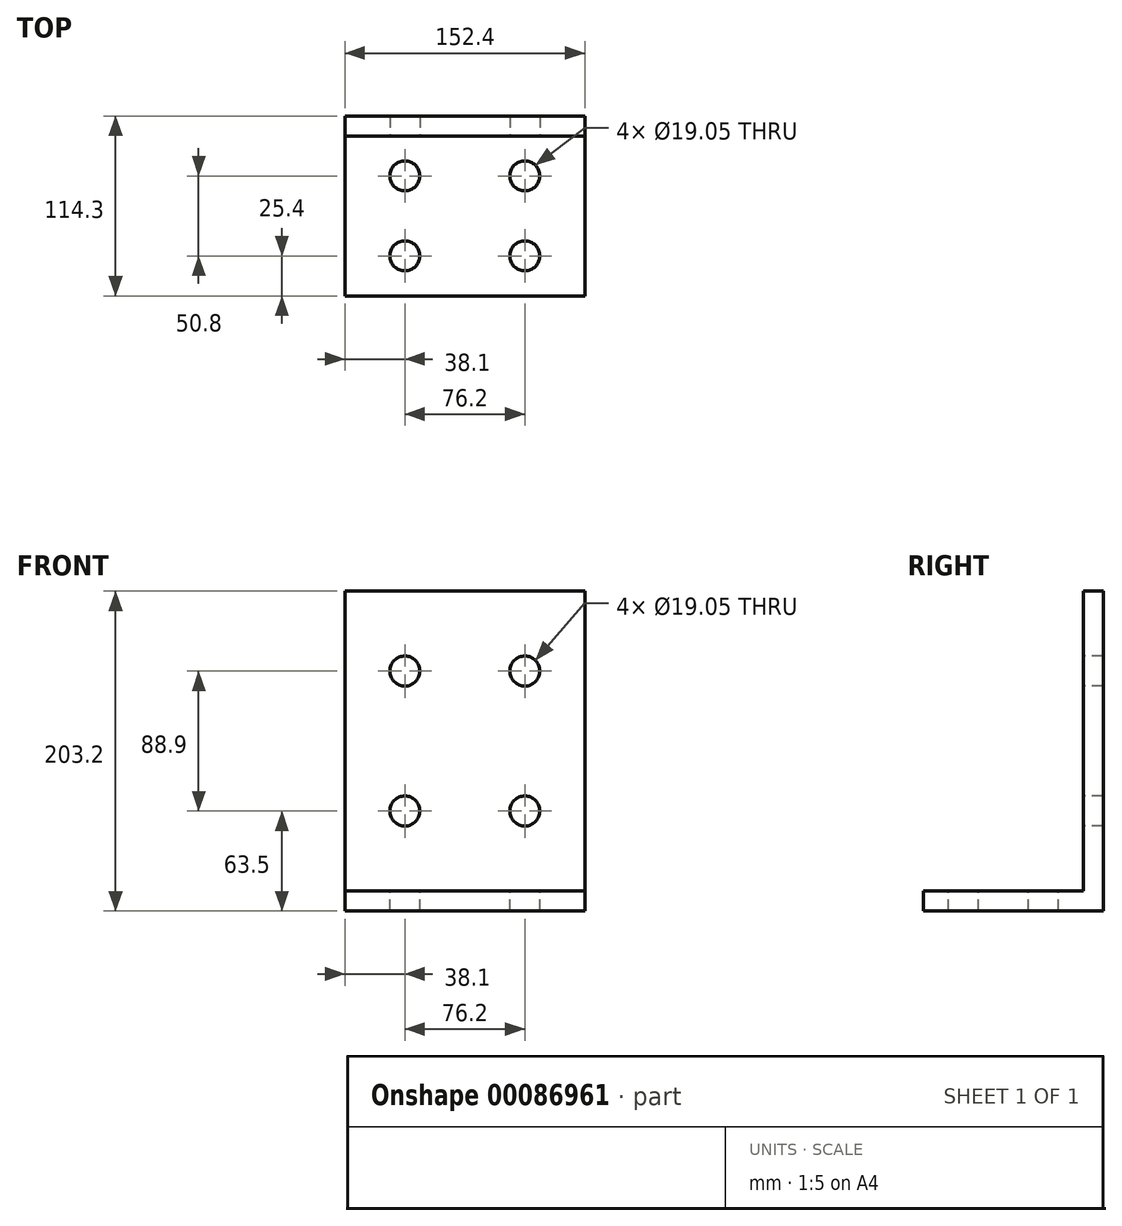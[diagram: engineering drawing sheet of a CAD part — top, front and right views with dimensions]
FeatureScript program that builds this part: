
annotation { "Feature Type Name" : "Feature", "Feature Type Description" : "" }
export const myFeature = defineFeature(function(context is Context, id is Id, definition is map)
    precondition{}
    {
        {
            var Q0;
            Q0=qCreatedBy(makeId("Front.planeOp"),FACE);
            var sketch = newSketch(context, id + "F0", { "sketchPlane" : qUnion([Q0])});
            skLineSegment(sketch, "E0.bottom", {"start": v(0, 0) * mm, "end": v(152.4, 0) * mm});
            skLineSegment(sketch, "E0.top", {"start": v(0, 203.2) * mm, "end": v(152.4, 203.2) * mm});
            skLineSegment(sketch, "E0.left", {"start": v(0, 0) * mm, "end": v(0, 203.2) * mm});
            skLineSegment(sketch, "E0.right", {"start": v(152.4, 0) * mm, "end": v(152.4, 203.2) * mm});
            skSolve(sketch);
        }
        {
            var Q0;
            Q0 = qSketchRegion(id + "F0", true);
            extrude(context, id + "F1", {"entities" : qUnion([Q0]), "depth" : 12.7 * mm});
        }
        {
            var Q0;
            Q0=makeQuery(id+"F1.opExtrude","CAP_FACE",FACE,{"disambiguationData":[OSD([sQuery(id+"F0.wireOp",EDGE,"E0.bottom"),sQuery(id+"F0.wireOp",EDGE,"E0.top"),sQuery(id+"F0.wireOp",EDGE,"E0.left"),sQuery(id+"F0.wireOp",EDGE,"E0.right")])],"isStart":false});
            var sketch = newSketch(context, id + "F2", { "sketchPlane" : qUnion([Q0])});
            skLineSegment(sketch, "E1.bottom", {"start": v(0, 0) * mm, "end": v(152.4, 0) * mm});
            skLineSegment(sketch, "E1.top", {"start": v(0, 12.7) * mm, "end": v(152.4, 12.7) * mm});
            skLineSegment(sketch, "E1.left", {"start": v(0, 0) * mm, "end": v(0, 12.7) * mm});
            skLineSegment(sketch, "E1.right", {"start": v(152.4, 0) * mm, "end": v(152.4, 12.7) * mm});
            skSolve(sketch);
        }
        {
            var Q0;
            Q0 = qSketchRegion(id + "F2", true);
            extrude(context, id + "F3", {"entities" : qUnion([Q0]), "operationType" : NewBodyOperationType.ADD, "depth" : 101.6 * mm});
        }
        {
            var Q0;
            Q0=makeQuery(id+"F3.opExtrude","SWEPT_FACE",FACE,{"disambiguationData":[OSD([sQuery(id+"F2.wireOp",EDGE,"E1.top")])]});
            var sketch = newSketch(context, id + "F4", { "sketchPlane" : qUnion([Q0])});
            skCircle(sketch, "E2", {"center": v(38.1, -88.9) * mm, "radius": 9.53 * mm});
            skSolve(sketch);
        }
        {
            var Q0;
            Q0=sQuery(id+"F4.wireOp",VERTEX,"E2.center");
            var Q1;
            Q1=makeQuery(id+"F1.opExtrude","SWEPT_BODY",BODY,{"disambiguationData":[OSD([sQuery(id+"F0.wireOp",EDGE,"E0.bottom"),sQuery(id+"F0.wireOp",EDGE,"E0.top"),sQuery(id+"F0.wireOp",EDGE,"E0.left"),sQuery(id+"F0.wireOp",EDGE,"E0.right")])]});
            hole(context, id + "F5", {"style" : HoleStyle.SIMPLE, "endStyle" : HoleEndStyle.BLIND, "holeDiameter" : 19.05 * mm, "holeDepth" : 12.7 * mm, "startFromSketch" : true, "locations" : qUnion([Q0]), "scope" : qUnion([Q1])});
        }
        {
            var Q0;
            Q0=makeQuery(id+"F3.opExtrude","SWEPT_FACE",FACE,{"disambiguationData":[OSD([sQuery(id+"F2.wireOp",EDGE,"E1.top")])]});
            var sketch = newSketch(context, id + "F6", { "sketchPlane" : qUnion([Q0])});
            skCircle(sketch, "E3", {"center": v(38.1, -38.1) * mm, "radius": 9.53 * mm});
            skCircle(sketch, "E4", {"center": v(114.3, -38.1) * mm, "radius": 9.53 * mm});
            skCircle(sketch, "E5", {"center": v(114.3, -88.9) * mm, "radius": 9.53 * mm});
            skSolve(sketch);
        }
        {
            var Q0;
            Q0=sQuery(id+"F6.wireOp",VERTEX,"E3.center");
            var Q1;
            Q1=sQuery(id+"F6.wireOp",VERTEX,"E4.center");
            var Q2;
            Q2=sQuery(id+"F6.wireOp",VERTEX,"E5.center");
            var Q3;
            Q3=makeQuery(id+"F1.opExtrude","SWEPT_BODY",BODY,{"disambiguationData":[OSD([sQuery(id+"F0.wireOp",EDGE,"E0.bottom"),sQuery(id+"F0.wireOp",EDGE,"E0.top"),sQuery(id+"F0.wireOp",EDGE,"E0.left"),sQuery(id+"F0.wireOp",EDGE,"E0.right")])]});
            hole(context, id + "F7", {"style" : HoleStyle.SIMPLE, "endStyle" : HoleEndStyle.BLIND, "holeDiameter" : 19.05 * mm, "holeDepth" : 12.7 * mm, "startFromSketch" : true, "locations" : qUnion([Q0, Q1, Q2]), "scope" : qUnion([Q3])});
        }
        {
            var Q0;
            Q0=makeQuery(id+"F1.opExtrude","CAP_FACE",FACE,{"disambiguationData":[OSD([sQuery(id+"F0.wireOp",EDGE,"E0.bottom"),sQuery(id+"F0.wireOp",EDGE,"E0.top"),sQuery(id+"F0.wireOp",EDGE,"E0.left"),sQuery(id+"F0.wireOp",EDGE,"E0.right")])],"isStart":false});
            var sketch = newSketch(context, id + "F8", { "sketchPlane" : qUnion([Q0])});
            skCircle(sketch, "E6", {"center": v(38.1, 152.4) * mm, "radius": 9.53 * mm});
            skCircle(sketch, "E7", {"center": v(38.1, 63.5) * mm, "radius": 9.53 * mm});
            skCircle(sketch, "E8", {"center": v(114.3, 152.4) * mm, "radius": 9.53 * mm});
            skCircle(sketch, "E9", {"center": v(114.3, 63.5) * mm, "radius": 9.53 * mm});
            skSolve(sketch);
        }
        {
            var Q0;
            Q0=sQuery(id+"F8.wireOp",VERTEX,"E6.center");
            var Q1;
            Q1=sQuery(id+"F8.wireOp",VERTEX,"E8.center");
            var Q2;
            Q2=sQuery(id+"F8.wireOp",VERTEX,"E9.center");
            var Q3;
            Q3=sQuery(id+"F8.wireOp",VERTEX,"E7.center");
            var Q4;
            Q4=makeQuery(id+"F1.opExtrude","SWEPT_BODY",BODY,{"disambiguationData":[OSD([sQuery(id+"F0.wireOp",EDGE,"E0.bottom"),sQuery(id+"F0.wireOp",EDGE,"E0.top"),sQuery(id+"F0.wireOp",EDGE,"E0.left"),sQuery(id+"F0.wireOp",EDGE,"E0.right")])]});
            hole(context, id + "F9", {"style" : HoleStyle.SIMPLE, "endStyle" : HoleEndStyle.BLIND, "holeDiameter" : 19.05 * mm, "holeDepth" : 12.7 * mm, "startFromSketch" : true, "locations" : qUnion([Q0, Q1, Q2, Q3]), "scope" : qUnion([Q4])});
        }
    });
